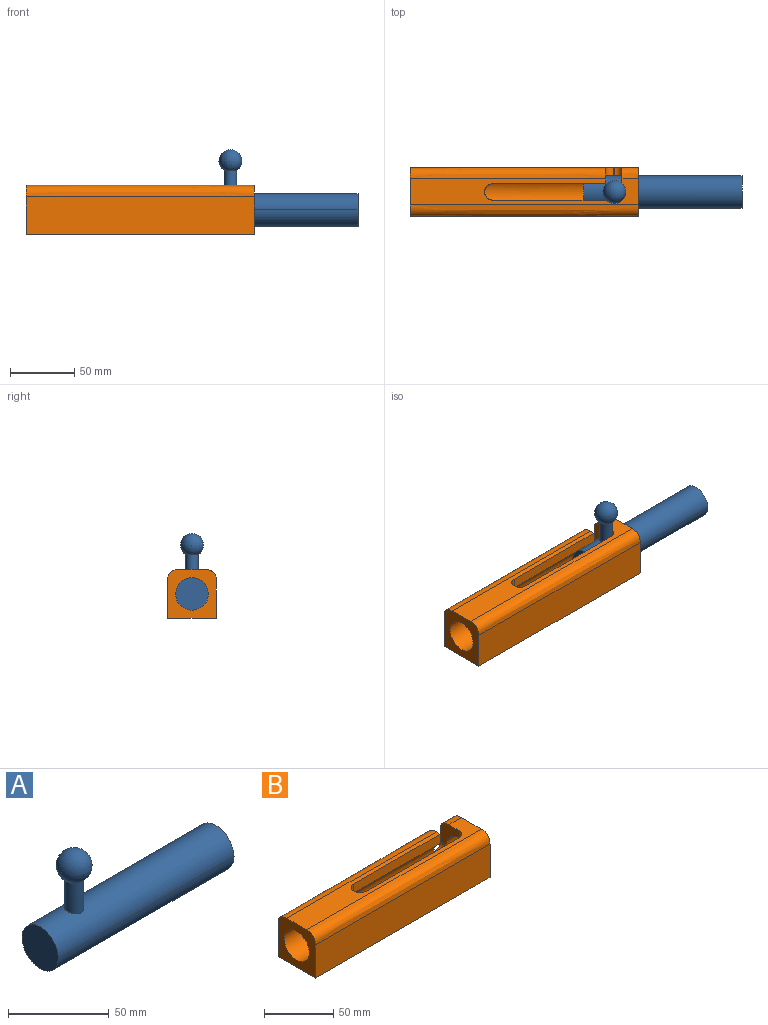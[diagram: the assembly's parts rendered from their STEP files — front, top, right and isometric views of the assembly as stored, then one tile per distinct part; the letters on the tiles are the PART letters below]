
ASSEMBLY  parts=2 mates=1
PART A: 6 faces, bbox 123.2x25.4x63.5 mm
  f0: cylinder r=12.7mm len=123.19mm, axis (-1,0,0), area 4840mm2, adj f1,f2,f3,f4
  f1: extruded ~123.19x25.4mm, area 4915.1mm2, adj f0,f2,f3
  f2: plane 29.21x25.4mm, normal (1,0,0), area 506.7mm2, adj f0,f1
  f3: plane 29.21x25.4mm, normal (-1,0,0), area 506.7mm2, adj f0,f1
  f4: cylinder r=4.84mm len=18.89mm, axis (0,0,-1), area 560.3mm2, adj f0,f5
  f5: sphere r=8.9mm, area 915.5mm2, adj f4
PART B: 21 faces, bbox 195.6x38.1x38.1 mm
  f0: plane 177.8x20.32mm, normal (0,0,1), area 2230.7mm2, adj f2,f4,f7,f8,f9,f10,f11,f13
  f1: cylinder r=12.7mm len=177.8mm, axis (-1,0,0), area 12556.3mm2, adj f2,f4,f7,f8,f9,f10,f11,f12
  f2: plane 38.1x38.1mm, normal (-1,0,0), area 918.6mm2, adj f0,f1,f3,f5,f6,f19,f20
  f3: plane 177.8x38.1mm, normal (0,0,-1), area 6774.2mm2, adj f2,f4,f5,f6
  f4: plane 38.1x38.1mm, normal (1,0,0), area 918.6mm2, adj f0,f1,f3,f5,f6,f18,f20
  f5: plane 177.8x29.21mm, normal (0,-1,0), area 5193.5mm2, adj f2,f3,f4,f20
  f6: plane 177.8x29.21mm, normal (0,1,0), area 4999.8mm2, adj f2,f3,f4,f7,f8,f12,f16,f17
  f7: plane 19.3x19.3mm, normal (-1,0,0), area 226.3mm2, adj f0,f1,f6,f15,f16,f18
  f8: plane 19.3x12.7mm, normal (1,0,0), area 180.8mm2, adj f0,f1,f6,f9,f17,f19
  f9: plane 88.11x8.05mm, normal (0,-1,0), area 709.4mm2, adj f0,f1,f8,f13
  f10: plane 6.35x0.51mm, normal (1,0,0), area 3.2mm2, adj f0,f1,f13,f14
  f11: plane 94.71x8.05mm, normal (0,1,0), area 762.6mm2, adj f0,f1,f14,f15
  f12: plane 8.05x0.51mm, normal (0,0,1), area 4.1mm2, adj f1,f6,f16,f17
  f13: cylinder r=6.1mm len=8.05mm, axis (0,0,1), area 69mm2, adj f0,f1,f9,f10
  f14: cylinder r=6.1mm len=8.05mm, axis (0,0,-1), area 69mm2, adj f0,f1,f10,f11
  f15: cylinder r=6.1mm len=8.05mm, axis (0,0,1), area 69mm2, adj f0,f1,f7,f11
  f16: cylinder r=6.1mm len=8.05mm, axis (0,1,0), area 69mm2, adj f1,f6,f7,f12
  f17: cylinder r=6.1mm len=8.05mm, axis (0,-1,0), area 69mm2, adj f1,f6,f8,f12
  f18: bspline ~13.97x8.89mm, area 183.3mm2, adj f0,f4,f6,f7
  f19: bspline ~167.64x8.89mm, area 2199.2mm2, adj f0,f2,f6,f8
  f20: bspline ~195.58x8.89mm, area 2565.7mm2, adj f0,f2,f4,f5
PLACE A t=(81.23,-10.38,-33.94)mm
PLACE B t=(0,-10.99,8.98)mm fixed
MATE cylindrical A.f0 <-> B.f1  axis (1,0,0) through (204.42,-30.04,4.03)mm
